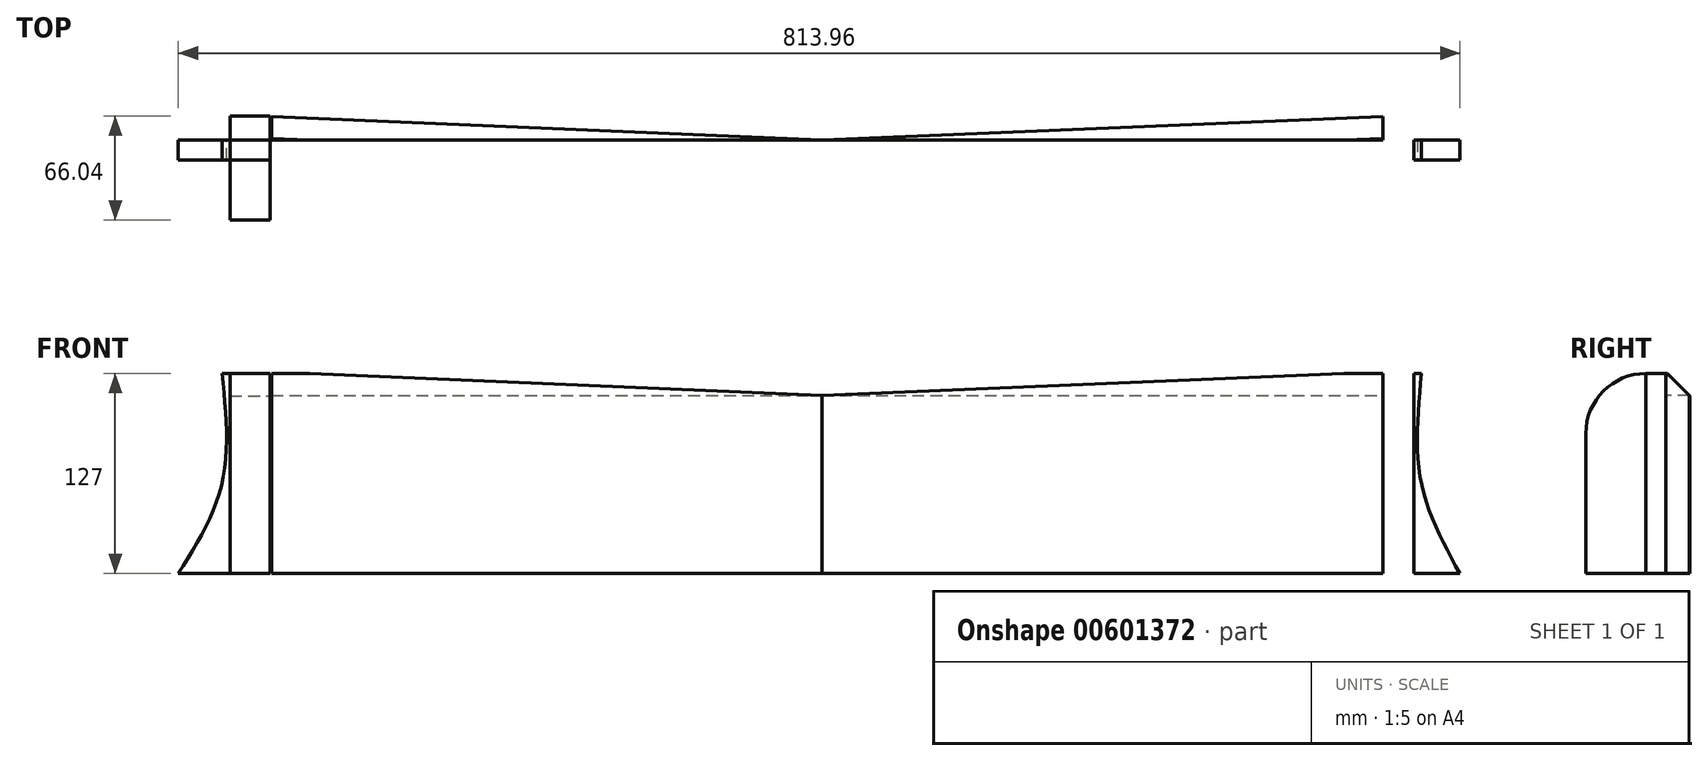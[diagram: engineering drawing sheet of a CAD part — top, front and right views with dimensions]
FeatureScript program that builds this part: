
annotation { "Feature Type Name" : "Feature", "Feature Type Description" : "" }
export const myFeature = defineFeature(function(context is Context, id is Id, definition is map)
    precondition{}
    {
        {
            var Q0;
            Q0=qCreatedBy(makeId("Front.planeOp"),FACE);
            var sketch = newSketch(context, id + "F0", { "sketchPlane" : qUnion([Q0])});
            skLineSegment(sketch, "E0", {"start": v(0, 0) * mm, "end": v(-381, 0) * mm});
            skLineSegment(sketch, "E1", {"start": v(0, 0) * mm, "end": v(380.83, 0) * mm});
            skLineSegment(sketch, "E2", {"start": v(-408.7, -127) * mm, "end": v(405.26, -127) * mm});
            skFitSpline(sketch, "E3", {"points": [v(-381, 0) * mm, v(-381, -69.86) * mm, v(-408.7, -127) * mm], "startDerivative": vector(14.54, -141.4) * mm, "endDerivative": vector(-70.64, -111.98) * mm});
            skFitSpline(sketch, "E4", {"points": [v(380.83, 0) * mm, v(380.83, -69.86) * mm, v(405.26, -127) * mm], "startDerivative": vector(-12.97, -140.35) * mm, "endDerivative": vector(62.58, -113) * mm});
            skSolve(sketch);
        }
        {
            var Q0;
            Q0=qCreatedBy(makeId("Right.planeOp"),FACE);
            var sketch = newSketch(context, id + "F1", { "sketchPlane" : qUnion([Q0])});
            skLineSegment(sketch, "E5", {"start": v(0, 0) * mm, "end": v(-50.8, 0) * mm});
            skLineSegment(sketch, "E6", {"start": v(-50.8, 0) * mm, "end": v(-50.8, -75.64) * mm});
            skLineSegment(sketch, "E7", {"start": v(0, 0) * mm, "end": v(15.24, -14.26) * mm});
            skLineSegment(sketch, "E8", {"start": v(15.24, -14.26) * mm, "end": v(15.24, -75.64) * mm});
            skLineSegment(sketch, "E9", {"start": v(-50.8, -75.64) * mm, "end": v(-50.8, -127) * mm});
            skLineSegment(sketch, "E10", {"start": v(-50.8, -127) * mm, "end": v(15.24, -127) * mm});
            skLineSegment(sketch, "E11", {"start": v(15.24, -75.64) * mm, "end": v(15.24, -127) * mm});
            skSolve(sketch);
        }
        {
            var Q0;
            Q0=makeQuery(id+"F0.imprint","IMPRINT",FACE,{"disambiguationData":[TD([[makeQuery(id+"F0.imprint","IMPRINT",EDGE,{"derivedFrom":sQuery(id+"F0.wireOp",EDGE,"E0")}),1.0]])]});
            extrude(context, id + "F2", {"entities" : qUnion([Q0]), "depth" : 12.7 * mm, "offsetDistance" : 25.4 * mm});
        }
        {
            var Q0;
            Q0=makeQuery(id+"F1.imprint","IMPRINT",FACE,{"disambiguationData":[TD([[makeQuery(id+"F1.imprint","IMPRINT",EDGE,{"derivedFrom":sQuery(id+"F1.wireOp",EDGE,"E5")}),1.0]])]});
            extrude(context, id + "F3", {"entities" : qUnion([Q0]), "depth" : 375.92 * mm, "offsetDistance" : 25.4 * mm});
        }
        {
            var Q0;
            Q0=makeQuery(id+"F3.opExtrude","CAP_FACE",FACE,{"disambiguationData":[OSD([sQuery(id+"F1.wireOp",EDGE,"E5"),sQuery(id+"F1.wireOp",EDGE,"E6"),sQuery(id+"F1.wireOp",EDGE,"E7"),sQuery(id+"F1.wireOp",EDGE,"E8"),sQuery(id+"F1.wireOp",EDGE,"E9"),sQuery(id+"F1.wireOp",EDGE,"E10"),sQuery(id+"F1.wireOp",EDGE,"E11")])],"isStart":true});
            extrude(context, id + "F4", {"entities" : qUnion([Q0]), "operationType" : NewBodyOperationType.REMOVE, "oppositeDirection" : true, "depth" : 355.6 * mm, "offsetDistance" : 25.4 * mm});
        }
        {
            var Q0;
            Q0=makeQuery(id+"F3.opExtrude","CAP_FACE",FACE,{"disambiguationData":[OSD([sQuery(id+"F1.wireOp",EDGE,"E5"),sQuery(id+"F1.wireOp",EDGE,"E6"),sQuery(id+"F1.wireOp",EDGE,"E7"),sQuery(id+"F1.wireOp",EDGE,"E8"),sQuery(id+"F1.wireOp",EDGE,"E9"),sQuery(id+"F1.wireOp",EDGE,"E10"),sQuery(id+"F1.wireOp",EDGE,"E11")])],"isStart":false});
            extrude(context, id + "F5", {"entities" : qUnion([Q0]), "oppositeDirection" : true, "depth" : 751.84 * mm, "offsetDistance" : 25.4 * mm});
        }
        {
            var Q0;
            Q0=makeQuery(id+"F3.opExtrude","CAP_FACE",FACE,{"disambiguationData":[OSD([sQuery(id+"F1.wireOp",EDGE,"E5"),sQuery(id+"F1.wireOp",EDGE,"E6"),sQuery(id+"F1.wireOp",EDGE,"E7"),sQuery(id+"F1.wireOp",EDGE,"E8"),sQuery(id+"F1.wireOp",EDGE,"E9"),sQuery(id+"F1.wireOp",EDGE,"E10"),sQuery(id+"F1.wireOp",EDGE,"E11")])],"isStart":false});
            extrude(context, id + "F6", {"entities" : qUnion([Q0]), "operationType" : NewBodyOperationType.REMOVE, "oppositeDirection" : true, "depth" : 726.44 * mm, "offsetDistance" : 25.4 * mm});
        }
        {
            var Q0;
            Q0=qCreatedBy(makeId("Top.planeOp"),FACE);
            var sketch = newSketch(context, id + "F7", { "sketchPlane" : qUnion([Q0])});
            skLineSegment(sketch, "E12", {"start": v(0, 0) * mm, "end": v(-349.52, 15.03) * mm});
            skLineSegment(sketch, "E13", {"start": v(-349.52, 15.03) * mm, "end": v(-349.52, 0) * mm});
            skLineSegment(sketch, "E14", {"start": v(-349.52, 0) * mm, "end": v(356.34, 0) * mm});
            skLineSegment(sketch, "E15", {"start": v(356.34, 0) * mm, "end": v(356.34, 15.03) * mm});
            skLineSegment(sketch, "E16", {"start": v(356.34, 15.03) * mm, "end": v(0, 0) * mm});
            skSolve(sketch);
        }
        {
            var Q0;
            Q0 = qSketchRegion(id + "F7", true);
            extrude(context, id + "F8", {"entities" : qUnion([Q0]), "oppositeDirection" : true, "depth" : 127 * mm, "offsetDistance" : 25.4 * mm});
        }
        {
            var Q0;
            Q0=makeQuery(id+"F8.opExtrude","CAP_EDGE",EDGE,{"disambiguationData":[OSD([sQuery(id+"F7.wireOp",EDGE,"E16")])],"isStart":true});
            var Q1;
            Q1=makeQuery(id+"F8.opExtrude","CAP_EDGE",EDGE,{"disambiguationData":[OSD([sQuery(id+"F7.wireOp",EDGE,"E12")])],"isStart":true});
            chamfer(context, id + "F9", {"entities" : qUnion([Q0, Q1]), "width" : 13.97 * mm, "tangentPropagation" : true});
        }
        {
            var Q0;
            Q0=makeQuery(id+"F5.opExtrude","SWEPT_EDGE",EDGE,{"disambiguationData":[OSD([sQuery(id+"F1.wireOp",EDGE,"E5"),sQuery(id+"F1.wireOp",EDGE,"E6")])]});
            var Q1;
            Q1=makeQuery(id+"F3.opExtrude","SWEPT_EDGE",EDGE,{"disambiguationData":[OSD([sQuery(id+"F1.wireOp",EDGE,"E5"),sQuery(id+"F1.wireOp",EDGE,"E6")])]});
            fillet(context, id + "F10", {"entities" : qUnion([Q0, Q1]), "radius" : 38.1 * mm, "tangentPropagation" : true, "allowEdgeOverflow" : false});
        }
    });
